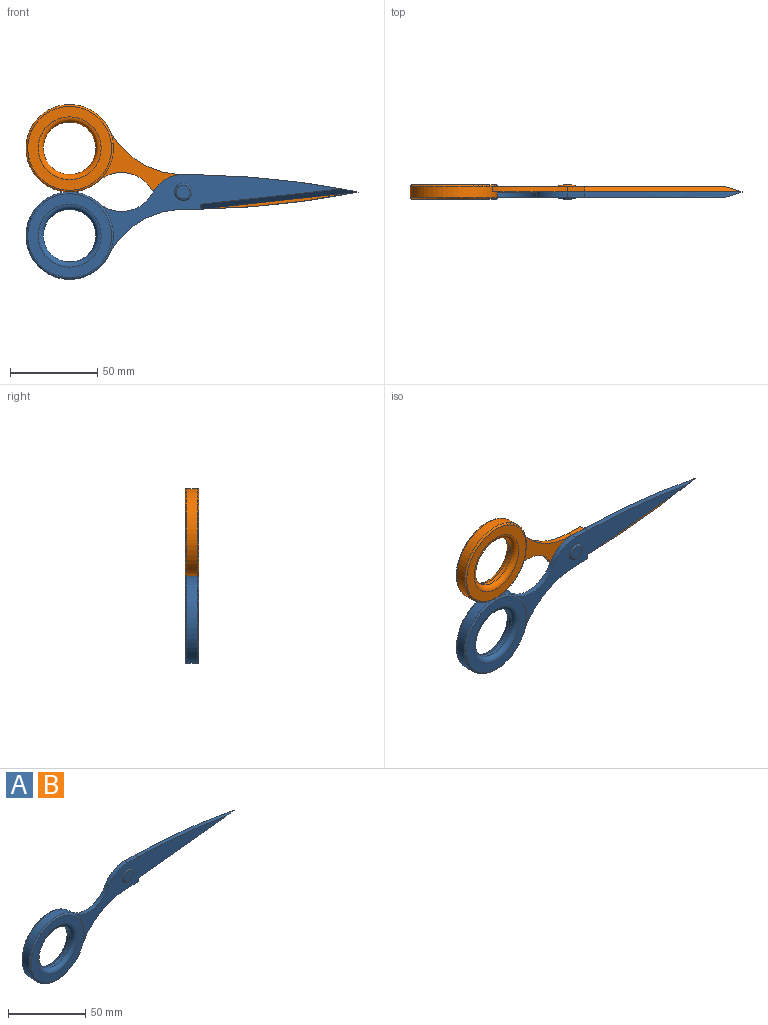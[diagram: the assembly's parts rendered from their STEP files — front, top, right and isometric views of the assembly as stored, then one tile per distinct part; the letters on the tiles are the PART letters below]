
ASSEMBLY  parts=2 mates=1
PART A: 21 faces, bbox 192.1x8x62.1 mm
  f0: plane 139.14x46.29mm, normal (0,-1,0), area 1500.3mm2, adj f2,f3,f5,f6,f7,f9,f14,f15
  f1: plane 148.5x46.29mm, normal (0,1,0), area 1819.6mm2, adj f2,f3,f4,f5,f6,f7,f8,f9
  f2: plane 10x3mm, normal (0.02,0,1), area 30mm2, adj f0,f1,f5,f6
  f3: plane 10x3mm, normal (0.02,0,-1), area 30mm2, adj f0,f1,f4,f9,f14
  f4: plane 90x9.82mm, normal (0.11,0,-0.99), area 16.3mm2, adj f1,f3,f5,f15
  f5: cylinder r=500mm len=90mm, axis (0,1,0), area 258.7mm2, adj f0,f1,f2,f4,f15
  f6: cylinder r=20mm len=17.65mm, axis (0,1,0), area 64.9mm2, adj f0,f1,f2,f7
  f7: cylinder r=20mm len=30.85mm, axis (0,1,0), area 108.1mm2, adj f0,f1,f6,f8
  f8: cylinder r=25mm len=50mm, axis (0,1,0), area 843.6mm2, adj f1,f7,f9,f18,f19
  f9: cylinder r=47.92mm len=42.69mm, axis (0,1,0), area 158.3mm2, adj f0,f1,f3,f8
  f10: plane 48x48mm, normal (0,1,0), area 791.7mm2, adj f17,f19
  f11: cylinder r=15mm len=30mm, axis (0,1,0), area 188.5mm2, adj f16,f17
  f12: plane 48x48mm, normal (0,-1,0), area 791.7mm2, adj f16,f18
  f13: plane 8x8mm, normal (0,-1,0), area 50.3mm2, adj f20
  f14: plane 2.82x2.82mm, normal (1,0,0), area 4mm2, adj f0,f3,f15
  f15: plane 90x11.62mm, normal (0.08,-0.71,-0.71), area 341.4mm2, adj f0,f4,f5,f14
  f16: torus R=18mm, axis (0,-1,0), area 476.4mm2, adj f11,f12
  f17: torus R=18mm, axis (0,-1,0), area 476.4mm2, adj f10,f11
  f18: torus R=24mm, axis (0,-1,0), area 243.2mm2, adj f0,f8,f12
  f19: torus R=24mm, axis (0,-1,0), area 243.2mm2, adj f8,f10
  f20: torus R=4mm, axis (0,-1,0), area 45.8mm2, adj f0,f13
PART B: same geometry as A
PLACE A t=(0.21,-13.66,-5)mm fixed
PLACE B rot(axis=(1,0,0),180deg) t=(0.21,-13.66,-5)mm
MATE revolute A.f20 <-> B.f20  axis (0,-1,0) through (0.21,-13.66,-5)mm
